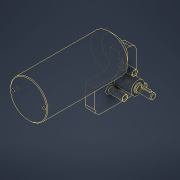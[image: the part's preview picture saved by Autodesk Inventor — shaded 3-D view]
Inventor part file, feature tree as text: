
AUTODESK INVENTOR PART (.ipt)
format: ipt  version: 2021 (Build 250183000, 183)  size: 284,672 bytes
history: native  units: mm
features: sketch x9, extrude x6, plane x5, chamfer x5, thread x3, projected_geometry x2, revolve x1, fillet x1, hole x1, other x1
ambient origin geometry x8: Origin, YZ Plane, XZ Plane, XY Plane, X Axis, Y Axis, Z Axis, Center Point
bodies: Solid1 (feature_tree)
feature tree (34):
  extrude  "Extrusion1"  Depth=139.0mm TaperAngle=0.0deg
  plane  "Work Plane1"
  plane  "Work Plane2"
  sketch  "Sketch2"  dims[d3=62.0mm d4=0.0mm]
  plane  "Work Plane3"
  sketch  "Sketch3"  dims[d5=0.0mm d6=62.0mm]
  extrude  "Extrusion2"  TaperAngle=0.0deg  [1 undecoded]
  revolve  "Revolution1"  [1 undecoded]
  plane  "Work Plane4"
  extrude  "Extrusion3"  Depth=15.0mm TaperAngle=0.0deg
  extrude  "Extrusion4"  Depth=99.5mm
  chamfer  "Chamfer1"  Distance=1.0mm
  fillet  "Fillet1"  Radius=2.0mm
  hole  "Hole1"  [1 undecoded]
  chamfer  "Chamfer3"  Distance=1.0mm
  chamfer  "Chamfer4"  Distance=4.0mm
  plane  "Work Plane5"
  extrude  "Extrusion5"  TaperAngle=0.0deg  [1 undecoded]
  chamfer  "Chamfer5"  Angle=90.0deg  [1 undecoded]
  extrude  "Extrusion6"  Depth=3.0mm
  thread  "Thread1"  [1 undecoded]
  thread  "Thread2"  [1 undecoded]
  thread  "Thread3"  [1 undecoded]
  chamfer  "Chamfer6"  Distance=30.0mm
  other  "calibration32"
  sketch  "Sketch1"  dims[d0=60.0mm d1=139.0mm d2=0.0mm]
  sketch  "Sketch4"  dims[d7=34.6mm d8=15.0mm d9=0.0mm]
  sketch  "Sketch5"  dims[d11=0.0mm d12=99.5mm]
  sketch  "Sketch6"  dims[d13=66.5mm]
  projected_geometry  "Projected Loop1"
  sketch  "Sketch7"  dims[d14=100.6mm]
  sketch  "Sketch8"  dims[d15=4.5mm]
  projected_geometry  "Projected Loop2"
  sketch  "Sketch9"  dims[d16=22.0mm d17=1.0mm d18=2.0mm d19=1.0mm d20=1.0mm d21=4.0mm d22=0.0mm d23=90.0deg d28=3.0mm d29=0.0mm d30=13.0mm d31=4.5mm d32=30.0mm d33=0.0mm d34=1.3mm d35=0.0mm d36=1.0mm d37=2.0mm d38=45.0deg d39=10.0mm d42=0.0mm d43=0.0mm d44=25.0mm d45=25.0mm d46=4.134mm d47=8.0mm d48=4.0mm d49=2.0mm d50=90.0deg d51=8.0mm d52=20.594885mm d56=9.0mm d57=2.0mm d58=45.0deg d59=1.0mm d60=2.0mm d61=45.0deg d62=-5.0mm d64=36.0mm d67=120.0deg d68=120.0deg d69=6.0mm d70=9.0mm d71=6.0mm d72=9.0mm d73=6.0mm d74=9.0mm d75=10.0mm d76=0.0mm d77=2.0mm d78=2.0mm d79=45.0deg d80=6.0mm d81=10.0mm d82=0.0mm d83=25.5mm d84=0.0mm d85=25.5mm d86=0.0mm d87=25.5mm d88=0.0mm d89=1.0mm d90=2.0mm d91=45.0deg d92=32.0mm]
note: 8 required parameter values undecoded (feature->parameter linkage not recoverable at this tier; creation-order binding heuristic only, values carry confidence <= 0.55)